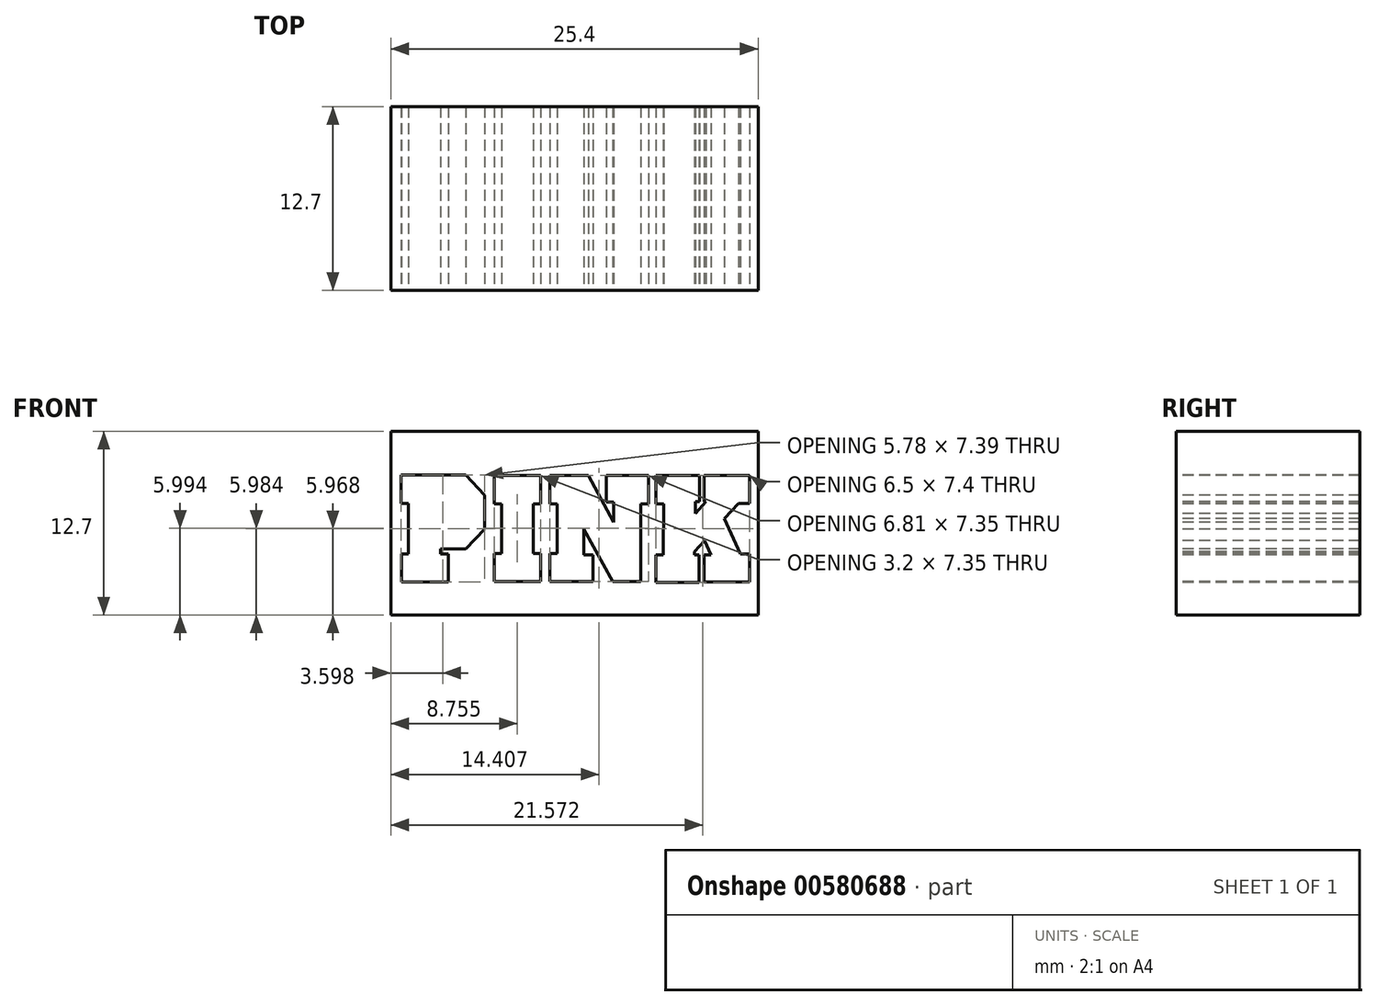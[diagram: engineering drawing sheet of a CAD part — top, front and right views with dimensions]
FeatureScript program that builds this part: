
annotation { "Feature Type Name" : "Feature", "Feature Type Description" : "" }
export const myFeature = defineFeature(function(context is Context, id is Id, definition is map)
    precondition{}
    {
        {
            var Q0;
            Q0=qCreatedBy(makeId("Front.planeOp"),FACE);
            var sketch = newSketch(context, id + "F0", { "sketchPlane" : qUnion([Q0])});
            skLineSegment(sketch, "E0", {"start": v(0, 0) * mm, "end": v(0, 25.4) * mm});
            skLineSegment(sketch, "E1", {"start": v(0, 25.4) * mm, "end": v(25.4, 25.4) * mm});
            skLineSegment(sketch, "E2", {"start": v(25.4, 25.4) * mm, "end": v(25.4, 0) * mm});
            skLineSegment(sketch, "E3", {"start": v(0, 0) * mm, "end": v(25.4, 0) * mm});
            skSolve(sketch);
        }
        {
            var Q0;
            Q0 = qSketchRegion(id + "F0", true);
            extrude(context, id + "F1", {"entities" : qUnion([Q0]), "depth" : 25.4 * mm, "offsetDistance" : 25.4 * mm});
        }
        {
            var Q0;
            Q0=makeQuery(id+"F1.opExtrude","CAP_FACE",FACE,{"disambiguationData":[OSD([sQuery(id+"F0.wireOp",EDGE,"E0"),sQuery(id+"F0.wireOp",EDGE,"E1"),sQuery(id+"F0.wireOp",EDGE,"E2"),sQuery(id+"F0.wireOp",EDGE,"E3")])],"isStart":false});
            var sketch = newSketch(context, id + "F2", { "sketchPlane" : qUnion([Q0])});
            skLineSegment(sketch, "E4", {"start": v(0.7, 9.68) * mm, "end": v(0.7, 7.71) * mm});
            skLineSegment(sketch, "E5", {"start": v(0.7, 7.71) * mm, "end": v(1.22, 7.71) * mm});
            skLineSegment(sketch, "E6", {"start": v(1.22, 7.71) * mm, "end": v(1.22, 4.23) * mm});
            skLineSegment(sketch, "E7", {"start": v(1.22, 4.23) * mm, "end": v(0.73, 4.23) * mm});
            skLineSegment(sketch, "E8", {"start": v(0.73, 4.23) * mm, "end": v(0.73, 2.29) * mm});
            skLineSegment(sketch, "E9", {"start": v(0.73, 2.29) * mm, "end": v(3.98, 2.29) * mm});
            skLineSegment(sketch, "E10", {"start": v(3.98, 2.29) * mm, "end": v(3.98, 4.23) * mm});
            skLineSegment(sketch, "E11", {"start": v(3.98, 4.23) * mm, "end": v(3.46, 4.23) * mm});
            skLineSegment(sketch, "E12", {"start": v(3.46, 4.23) * mm, "end": v(3.46, 4.57) * mm});
            skLineSegment(sketch, "E13", {"start": v(3.46, 4.57) * mm, "end": v(5.19, 4.57) * mm});
            skLineSegment(sketch, "E14", {"start": v(5.19, 4.57) * mm, "end": v(6.49, 5.94) * mm});
            skLineSegment(sketch, "E15", {"start": v(6.49, 5.94) * mm, "end": v(6.49, 8.28) * mm});
            skLineSegment(sketch, "E16", {"start": v(6.49, 8.28) * mm, "end": v(5.19, 9.68) * mm});
            skLineSegment(sketch, "E17", {"start": v(5.19, 9.68) * mm, "end": v(0.7, 9.68) * mm});
            skLineSegment(sketch, "E18", {"start": v(7.15, 9.67) * mm, "end": v(10.36, 9.67) * mm});
            skLineSegment(sketch, "E19", {"start": v(10.36, 9.67) * mm, "end": v(10.36, 7.7) * mm});
            skLineSegment(sketch, "E20", {"start": v(10.36, 7.7) * mm, "end": v(9.86, 7.7) * mm});
            skLineSegment(sketch, "E21", {"start": v(9.86, 7.7) * mm, "end": v(9.86, 4.26) * mm});
            skLineSegment(sketch, "E22", {"start": v(9.86, 4.26) * mm, "end": v(10.36, 4.26) * mm});
            skLineSegment(sketch, "E23", {"start": v(10.36, 4.26) * mm, "end": v(10.36, 2.32) * mm});
            skLineSegment(sketch, "E24", {"start": v(10.36, 2.32) * mm, "end": v(7.16, 2.32) * mm});
            skLineSegment(sketch, "E25", {"start": v(7.16, 2.32) * mm, "end": v(7.16, 4.26) * mm});
            skLineSegment(sketch, "E26", {"start": v(7.16, 4.26) * mm, "end": v(7.65, 4.26) * mm});
            skLineSegment(sketch, "E27", {"start": v(7.65, 4.26) * mm, "end": v(7.65, 7.69) * mm});
            skLineSegment(sketch, "E28", {"start": v(7.65, 7.69) * mm, "end": v(7.16, 7.69) * mm});
            skLineSegment(sketch, "E29", {"start": v(7.16, 7.69) * mm, "end": v(7.15, 9.67) * mm});
            skLineSegment(sketch, "E30", {"start": v(11, 9.67) * mm, "end": v(11, 7.69) * mm});
            skLineSegment(sketch, "E31", {"start": v(11, 7.69) * mm, "end": v(11.51, 7.69) * mm});
            skLineSegment(sketch, "E32", {"start": v(11.51, 7.69) * mm, "end": v(11.51, 4.26) * mm});
            skLineSegment(sketch, "E33", {"start": v(11.51, 4.26) * mm, "end": v(11, 4.26) * mm});
            skLineSegment(sketch, "E34", {"start": v(11, 4.26) * mm, "end": v(11, 2.32) * mm});
            skLineSegment(sketch, "E35", {"start": v(11, 2.32) * mm, "end": v(13.99, 2.32) * mm});
            skLineSegment(sketch, "E36", {"start": v(13.99, 2.32) * mm, "end": v(13.99, 4.17) * mm});
            skLineSegment(sketch, "E37", {"start": v(13.99, 4.17) * mm, "end": v(13.35, 4.17) * mm});
            skLineSegment(sketch, "E38", {"start": v(13.35, 4.17) * mm, "end": v(13.35, 5.94) * mm});
            skLineSegment(sketch, "E39", {"start": v(13.35, 5.94) * mm, "end": v(15.34, 2.32) * mm});
            skLineSegment(sketch, "E40", {"start": v(15.34, 2.32) * mm, "end": v(17.28, 2.32) * mm});
            skLineSegment(sketch, "E41", {"start": v(17.28, 2.32) * mm, "end": v(17.28, 7.69) * mm});
            skLineSegment(sketch, "E42", {"start": v(17.28, 7.69) * mm, "end": v(17.81, 7.69) * mm});
            skLineSegment(sketch, "E43", {"start": v(17.81, 7.69) * mm, "end": v(17.81, 9.67) * mm});
            skLineSegment(sketch, "E44", {"start": v(17.81, 9.67) * mm, "end": v(14.9, 9.67) * mm});
            skLineSegment(sketch, "E45", {"start": v(14.9, 9.67) * mm, "end": v(14.9, 7.8) * mm});
            skLineSegment(sketch, "E46", {"start": v(14.9, 7.8) * mm, "end": v(15.4, 7.8) * mm});
            skLineSegment(sketch, "E47", {"start": v(15.4, 7.8) * mm, "end": v(15.4, 6.42) * mm});
            skLineSegment(sketch, "E48", {"start": v(15.4, 6.42) * mm, "end": v(13.68, 9.67) * mm});
            skLineSegment(sketch, "E49", {"start": v(13.68, 9.67) * mm, "end": v(11, 9.67) * mm});
            skLineSegment(sketch, "E50", {"start": v(18.33, 9.67) * mm, "end": v(21.36, 9.67) * mm});
            skLineSegment(sketch, "E51", {"start": v(21.36, 9.67) * mm, "end": v(21.36, 7.84) * mm});
            skLineSegment(sketch, "E52", {"start": v(21.36, 7.84) * mm, "end": v(21.07, 7.84) * mm});
            skLineSegment(sketch, "E53", {"start": v(21.07, 7.84) * mm, "end": v(21.07, 7.03) * mm});
            skLineSegment(sketch, "E54", {"start": v(21.07, 7.03) * mm, "end": v(21.8, 7.86) * mm});
            skLineSegment(sketch, "E55", {"start": v(21.8, 7.86) * mm, "end": v(21.66, 7.86) * mm});
            skLineSegment(sketch, "E56", {"start": v(21.66, 7.86) * mm, "end": v(21.66, 9.65) * mm});
            skLineSegment(sketch, "E57", {"start": v(21.66, 9.65) * mm, "end": v(24.82, 9.65) * mm});
            skLineSegment(sketch, "E58", {"start": v(24.82, 9.65) * mm, "end": v(24.82, 7.7) * mm});
            skLineSegment(sketch, "E59", {"start": v(24.82, 7.7) * mm, "end": v(24.05, 7.7) * mm});
            skLineSegment(sketch, "E60", {"start": v(24.05, 7.7) * mm, "end": v(23.05, 6.67) * mm});
            skLineSegment(sketch, "E61", {"start": v(23.05, 6.67) * mm, "end": v(24.17, 4.23) * mm});
            skLineSegment(sketch, "E62", {"start": v(24.17, 4.23) * mm, "end": v(24.82, 4.23) * mm});
            skLineSegment(sketch, "E63", {"start": v(24.82, 4.23) * mm, "end": v(24.82, 2.28) * mm});
            skLineSegment(sketch, "E64", {"start": v(24.82, 2.28) * mm, "end": v(21.66, 2.28) * mm});
            skLineSegment(sketch, "E65", {"start": v(21.66, 2.28) * mm, "end": v(21.66, 4.18) * mm});
            skLineSegment(sketch, "E66", {"start": v(21.66, 4.18) * mm, "end": v(22.14, 4.18) * mm});
            skLineSegment(sketch, "E67", {"start": v(22.14, 4.18) * mm, "end": v(21.7, 5.14) * mm});
            skLineSegment(sketch, "E68", {"start": v(21.7, 5.14) * mm, "end": v(21, 4.4) * mm});
            skLineSegment(sketch, "E69", {"start": v(21, 4.4) * mm, "end": v(21, 4.18) * mm});
            skLineSegment(sketch, "E70", {"start": v(21, 4.18) * mm, "end": v(21.31, 4.18) * mm});
            skLineSegment(sketch, "E71", {"start": v(21.31, 4.18) * mm, "end": v(21.31, 2.27) * mm});
            skLineSegment(sketch, "E72", {"start": v(21.31, 2.27) * mm, "end": v(18.32, 2.27) * mm});
            skLineSegment(sketch, "E73", {"start": v(18.32, 2.27) * mm, "end": v(18.32, 4.18) * mm});
            skLineSegment(sketch, "E74", {"start": v(18.32, 4.18) * mm, "end": v(18.85, 4.18) * mm});
            skLineSegment(sketch, "E75", {"start": v(18.85, 4.18) * mm, "end": v(18.87, 7.69) * mm});
            skLineSegment(sketch, "E76", {"start": v(18.87, 7.69) * mm, "end": v(18.32, 7.69) * mm});
            skLineSegment(sketch, "E77", {"start": v(18.32, 7.69) * mm, "end": v(18.33, 9.67) * mm});
            skLineSegment(sketch, "E78", {"start": v(1.37, 9.06) * mm, "end": v(1.37, 8.3) * mm});
            skLineSegment(sketch, "E79", {"start": v(1.37, 8.3) * mm, "end": v(1.9, 8.3) * mm});
            skLineSegment(sketch, "E80", {"start": v(1.9, 8.3) * mm, "end": v(1.9, 3.62) * mm});
            skLineSegment(sketch, "E81", {"start": v(1.9, 3.62) * mm, "end": v(1.37, 3.62) * mm});
            skLineSegment(sketch, "E82", {"start": v(1.37, 3.62) * mm, "end": v(1.37, 2.93) * mm});
            skLineSegment(sketch, "E83", {"start": v(1.37, 2.93) * mm, "end": v(3.28, 2.93) * mm});
            skLineSegment(sketch, "E84", {"start": v(3.28, 2.93) * mm, "end": v(3.28, 3.62) * mm});
            skLineSegment(sketch, "E85", {"start": v(3.28, 3.62) * mm, "end": v(2.83, 3.62) * mm});
            skLineSegment(sketch, "E86", {"start": v(2.83, 3.62) * mm, "end": v(2.83, 5.23) * mm});
            skLineSegment(sketch, "E87", {"start": v(2.83, 5.23) * mm, "end": v(4.94, 5.23) * mm});
            skLineSegment(sketch, "E88", {"start": v(4.94, 5.23) * mm, "end": v(5.84, 6.18) * mm});
            skLineSegment(sketch, "E89", {"start": v(5.84, 6.18) * mm, "end": v(5.84, 8.1) * mm});
            skLineSegment(sketch, "E90", {"start": v(5.84, 8.1) * mm, "end": v(4.9, 9.02) * mm});
            skLineSegment(sketch, "E91", {"start": v(4.9, 9.02) * mm, "end": v(1.37, 9.06) * mm});
            skLineSegment(sketch, "E92", {"start": v(7.8, 9.04) * mm, "end": v(7.8, 8.34) * mm});
            skLineSegment(sketch, "E93", {"start": v(7.8, 8.34) * mm, "end": v(8.35, 8.35) * mm});
            skLineSegment(sketch, "E94", {"start": v(8.35, 8.35) * mm, "end": v(8.35, 3.64) * mm});
            skLineSegment(sketch, "E95", {"start": v(8.35, 3.64) * mm, "end": v(7.79, 3.63) * mm});
            skLineSegment(sketch, "E96", {"start": v(7.79, 3.63) * mm, "end": v(7.8, 2.9) * mm});
            skLineSegment(sketch, "E97", {"start": v(7.8, 2.9) * mm, "end": v(9.72, 2.9) * mm});
            skLineSegment(sketch, "E98", {"start": v(9.72, 2.9) * mm, "end": v(9.7, 3.62) * mm});
            skLineSegment(sketch, "E99", {"start": v(9.7, 3.62) * mm, "end": v(9.19, 3.61) * mm});
            skLineSegment(sketch, "E100", {"start": v(9.19, 3.61) * mm, "end": v(9.16, 8.33) * mm});
            skLineSegment(sketch, "E101", {"start": v(9.16, 8.33) * mm, "end": v(9.7, 8.33) * mm});
            skLineSegment(sketch, "E102", {"start": v(9.7, 8.33) * mm, "end": v(9.7, 9.04) * mm});
            skLineSegment(sketch, "E103", {"start": v(9.7, 9.04) * mm, "end": v(7.8, 9.04) * mm});
            skLineSegment(sketch, "E104", {"start": v(11.66, 9.04) * mm, "end": v(11.66, 8.33) * mm});
            skLineSegment(sketch, "E105", {"start": v(11.66, 8.33) * mm, "end": v(12.14, 8.33) * mm});
            skLineSegment(sketch, "E106", {"start": v(12.14, 8.33) * mm, "end": v(12.17, 3.59) * mm});
            skLineSegment(sketch, "E107", {"start": v(12.17, 3.59) * mm, "end": v(11.68, 3.59) * mm});
            skLineSegment(sketch, "E108", {"start": v(11.68, 3.59) * mm, "end": v(11.68, 2.96) * mm});
            skLineSegment(sketch, "E109", {"start": v(11.68, 2.96) * mm, "end": v(13.38, 2.97) * mm});
            skLineSegment(sketch, "E110", {"start": v(13.38, 2.97) * mm, "end": v(13.37, 3.65) * mm});
            skLineSegment(sketch, "E111", {"start": v(13.37, 3.65) * mm, "end": v(12.93, 3.65) * mm});
            skLineSegment(sketch, "E112", {"start": v(12.93, 3.65) * mm, "end": v(12.9, 8.12) * mm});
            skLineSegment(sketch, "E113", {"start": v(12.9, 8.12) * mm, "end": v(15.74, 2.96) * mm});
            skLineSegment(sketch, "E114", {"start": v(15.74, 2.96) * mm, "end": v(16.61, 2.97) * mm});
            skLineSegment(sketch, "E115", {"start": v(16.61, 2.97) * mm, "end": v(16.58, 8.33) * mm});
            skLineSegment(sketch, "E116", {"start": v(16.58, 8.33) * mm, "end": v(17.22, 8.34) * mm});
            skLineSegment(sketch, "E117", {"start": v(17.22, 8.34) * mm, "end": v(17.21, 9.03) * mm});
            skLineSegment(sketch, "E118", {"start": v(17.21, 9.03) * mm, "end": v(15.52, 9) * mm});
            skLineSegment(sketch, "E119", {"start": v(15.52, 9) * mm, "end": v(15.53, 8.33) * mm});
            skLineSegment(sketch, "E120", {"start": v(15.53, 8.33) * mm, "end": v(15.99, 8.34) * mm});
            skLineSegment(sketch, "E121", {"start": v(15.99, 8.34) * mm, "end": v(15.99, 4.24) * mm});
            skLineSegment(sketch, "E122", {"start": v(15.99, 4.24) * mm, "end": v(13.26, 9) * mm});
            skLineSegment(sketch, "E123", {"start": v(13.26, 9) * mm, "end": v(11.66, 9.04) * mm});
            skLineSegment(sketch, "E124", {"start": v(19, 9.04) * mm, "end": v(19, 8.33) * mm});
            skLineSegment(sketch, "E125", {"start": v(19, 8.33) * mm, "end": v(19.5, 8.33) * mm});
            skLineSegment(sketch, "E126", {"start": v(19.5, 8.33) * mm, "end": v(19.52, 3.59) * mm});
            skLineSegment(sketch, "E127", {"start": v(19.52, 3.59) * mm, "end": v(19, 3.59) * mm});
            skLineSegment(sketch, "E128", {"start": v(19, 3.59) * mm, "end": v(19, 2.93) * mm});
            skLineSegment(sketch, "E129", {"start": v(19, 2.93) * mm, "end": v(20.68, 2.94) * mm});
            skLineSegment(sketch, "E130", {"start": v(20.68, 2.94) * mm, "end": v(20.68, 3.59) * mm});
            skLineSegment(sketch, "E131", {"start": v(20.68, 3.59) * mm, "end": v(20.41, 3.59) * mm});
            skLineSegment(sketch, "E132", {"start": v(20.41, 3.59) * mm, "end": v(20.41, 4.64) * mm});
            skLineSegment(sketch, "E133", {"start": v(20.41, 4.64) * mm, "end": v(21.75, 6.2) * mm});
            skLineSegment(sketch, "E134", {"start": v(21.75, 6.2) * mm, "end": v(22.95, 3.59) * mm});
            skLineSegment(sketch, "E135", {"start": v(22.95, 3.59) * mm, "end": v(22.35, 3.59) * mm});
            skLineSegment(sketch, "E136", {"start": v(22.35, 3.59) * mm, "end": v(22.35, 2.96) * mm});
            skLineSegment(sketch, "E137", {"start": v(22.35, 2.96) * mm, "end": v(24.18, 2.96) * mm});
            skLineSegment(sketch, "E138", {"start": v(24.18, 2.96) * mm, "end": v(24.18, 3.59) * mm});
            skLineSegment(sketch, "E139", {"start": v(24.18, 3.59) * mm, "end": v(23.7, 3.59) * mm});
            skLineSegment(sketch, "E140", {"start": v(23.7, 3.59) * mm, "end": v(22.35, 6.74) * mm});
            skLineSegment(sketch, "E141", {"start": v(22.35, 6.74) * mm, "end": v(23.73, 8.31) * mm});
            skLineSegment(sketch, "E142", {"start": v(23.73, 8.31) * mm, "end": v(24.18, 8.31) * mm});
            skLineSegment(sketch, "E143", {"start": v(24.18, 8.31) * mm, "end": v(24.18, 9.04) * mm});
            skLineSegment(sketch, "E144", {"start": v(24.18, 9.04) * mm, "end": v(22.35, 9.04) * mm});
            skLineSegment(sketch, "E145", {"start": v(22.35, 9.04) * mm, "end": v(22.35, 8.34) * mm});
            skLineSegment(sketch, "E146", {"start": v(22.35, 8.34) * mm, "end": v(22.95, 8.34) * mm});
            skLineSegment(sketch, "E147", {"start": v(22.95, 8.34) * mm, "end": v(20.41, 5.55) * mm});
            skLineSegment(sketch, "E148", {"start": v(20.41, 5.55) * mm, "end": v(20.41, 8.3) * mm});
            skLineSegment(sketch, "E149", {"start": v(20.41, 8.3) * mm, "end": v(20.67, 8.3) * mm});
            skLineSegment(sketch, "E150", {"start": v(20.67, 8.3) * mm, "end": v(20.67, 9.04) * mm});
            skLineSegment(sketch, "E151", {"start": v(20.67, 9.04) * mm, "end": v(19, 9.04) * mm});
            skSolve(sketch);
        }
        {
            var Q0;
            Q0 = qSketchRegion(id + "F2", true);
            var Q1;
            Q1=makeQuery(id+"F2.imprint","IMPRINT",FACE,{"disambiguationData":[TD([[makeQuery(id+"F2.imprint","IMPRINT",EDGE,{"derivedFrom":sQuery(id+"F2.wireOp",EDGE,"E78")}),1.0]])]});
            var Q2;
            Q2=makeQuery(id+"F2.imprint","IMPRINT",FACE,{"disambiguationData":[TD([[makeQuery(id+"F2.imprint","IMPRINT",EDGE,{"derivedFrom":sQuery(id+"F2.wireOp",EDGE,"E92")}),1.0]])]});
            var Q3;
            Q3=makeQuery(id+"F2.imprint","IMPRINT",FACE,{"disambiguationData":[TD([[makeQuery(id+"F2.imprint","IMPRINT",EDGE,{"derivedFrom":sQuery(id+"F2.wireOp",EDGE,"E104")}),1.0]])]});
            var Q4;
            Q4=makeQuery(id+"F2.imprint","IMPRINT",FACE,{"disambiguationData":[TD([[makeQuery(id+"F2.imprint","IMPRINT",EDGE,{"derivedFrom":sQuery(id+"F2.wireOp",EDGE,"E124")}),1.0]])]});
            extrude(context, id + "F3", {"entities" : qUnion([Q0, Q1, Q2, Q3, Q4]), "operationType" : NewBodyOperationType.REMOVE, "oppositeDirection" : true, "depth" : 25.4 * mm, "offsetDistance" : 25.4 * mm});
        }
        {
            var Q0;
            Q0=makeQuery(id+"F1.opExtrude","CAP_FACE",FACE,{"disambiguationData":[OSD([sQuery(id+"F0.wireOp",EDGE,"E0"),sQuery(id+"F0.wireOp",EDGE,"E1"),sQuery(id+"F0.wireOp",EDGE,"E2"),sQuery(id+"F0.wireOp",EDGE,"E3")])],"isStart":false});
            var sketch = newSketch(context, id + "F4", { "sketchPlane" : qUnion([Q0])});
            skLineSegment(sketch, "E152", {"start": v(0, 12.7) * mm, "end": v(25.4, 12.7) * mm});
            skSolve(sketch);
        }
        {
            var Q0;
            {var subQ0=sQuery(id+"F4.wireOp",EDGE,"E152");Q0=makeQuery(id+"F4.imprint","IMPRINT",FACE,{"disambiguationData":[TD([[makeQuery(id+"F4.imprint","IMPRINT",EDGE,{"derivedFrom":subQ0}),1.0]])]});}
            extrude(context, id + "F5", {"entities" : qUnion([Q0]), "operationType" : NewBodyOperationType.REMOVE, "oppositeDirection" : true, "depth" : 25.4 * mm, "offsetDistance" : 25.4 * mm});
        }
        {
            var Q0;
            Q0=makeQuery(id+"F1.opExtrude","SWEPT_FACE",FACE,{"disambiguationData":[OSD([sQuery(id+"F0.wireOp",EDGE,"E0")])]});
            var sketch = newSketch(context, id + "F6", { "sketchPlane" : qUnion([Q0])});
            skLineSegment(sketch, "E153", {"start": v(12.7, 12.7) * mm, "end": v(12.7, 0) * mm});
            skSolve(sketch);
        }
        {
            var Q0;
            {var subQ0=sQuery(id+"F6.wireOp",EDGE,"E153");Q0=makeQuery(id+"F6.imprint","IMPRINT",FACE,{"disambiguationData":[TD([[makeQuery(id+"F6.imprint","IMPRINT",EDGE,{"derivedFrom":subQ0}),1.0]])]});}
            extrude(context, id + "F7", {"entities" : qUnion([Q0]), "operationType" : NewBodyOperationType.REMOVE, "oppositeDirection" : true, "depth" : 25.4 * mm, "offsetDistance" : 25.4 * mm});
        }
    });
